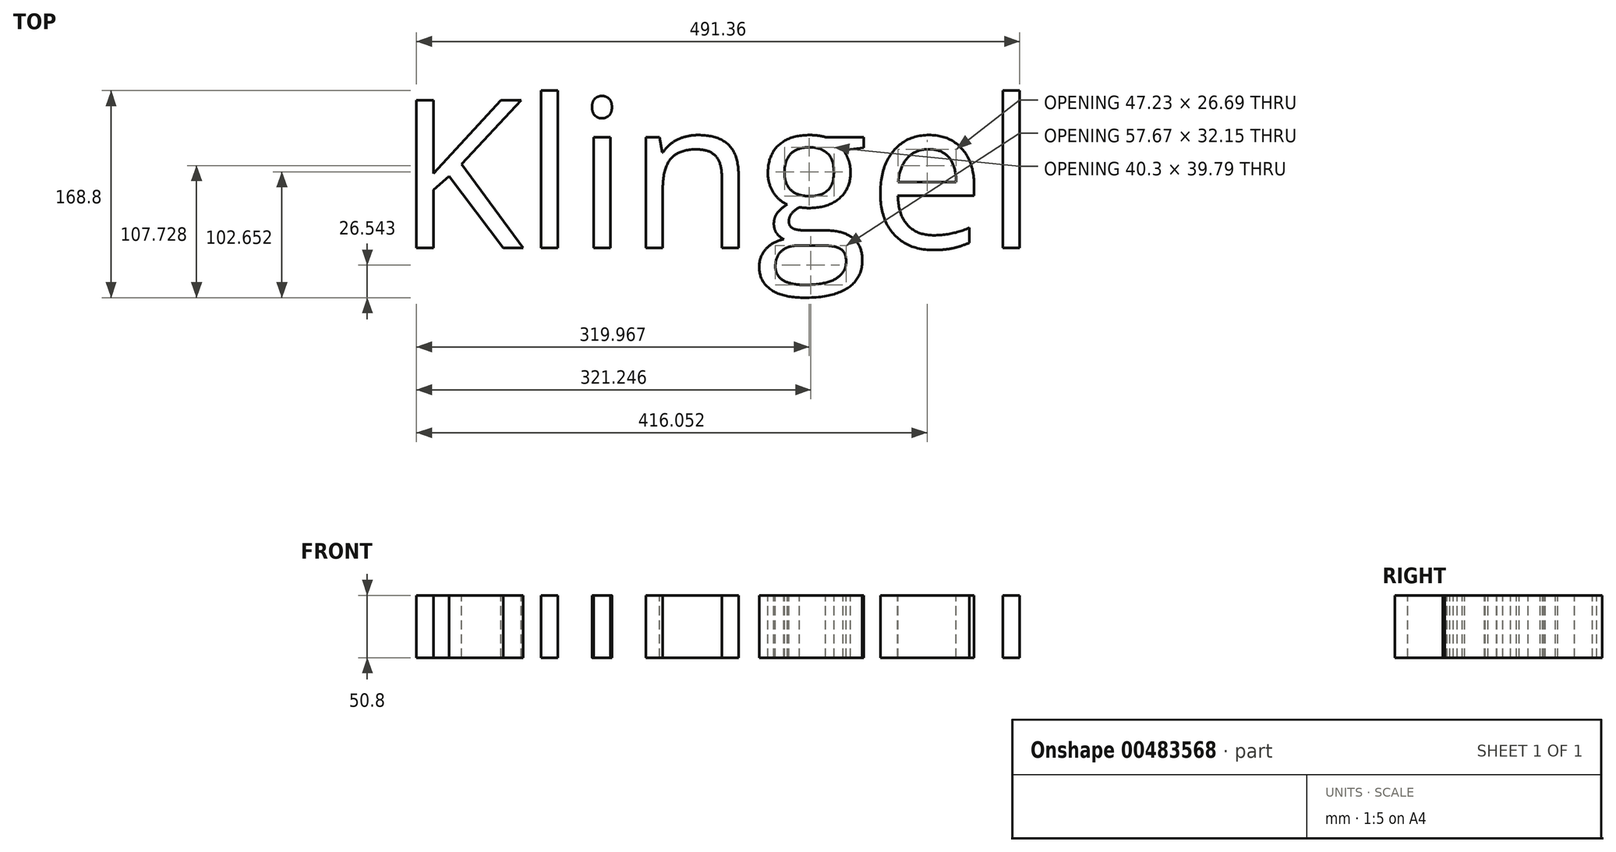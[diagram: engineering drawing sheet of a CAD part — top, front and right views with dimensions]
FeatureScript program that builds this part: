
annotation { "Feature Type Name" : "Feature", "Feature Type Description" : "" }
export const myFeature = defineFeature(function(context is Context, id is Id, definition is map)
    precondition{}
    {
        {
            var Q0;
            Q0=qCreatedBy(makeId("Top.planeOp"),FACE);
            var sketch = newSketch(context, id + "F0", { "sketchPlane" : qUnion([Q0])});
            skText(sketch, "E0", { "text": "Klingel", "fontName": "OpenSans-Regular.ttf"});
            const initialGuessF0  = {"E0": [-0.0489, -0.00984, 1, 0, 0.12152]};
            skSetInitialGuess(sketch, initialGuessF0);
            skSolve(sketch);
        }
        {
            var Q0;
            Q0 = qSketchRegion(id + "F0", true);
            extrude(context, id + "F1", {"entities" : qUnion([Q0]), "oppositeDirection" : true, "depth" : 25.4 * mm, "hasSecondDirection" : true, "secondDirectionOppositeDirection" : false, "secondDirectionDepth" : 25.4 * mm});
        }
    });
